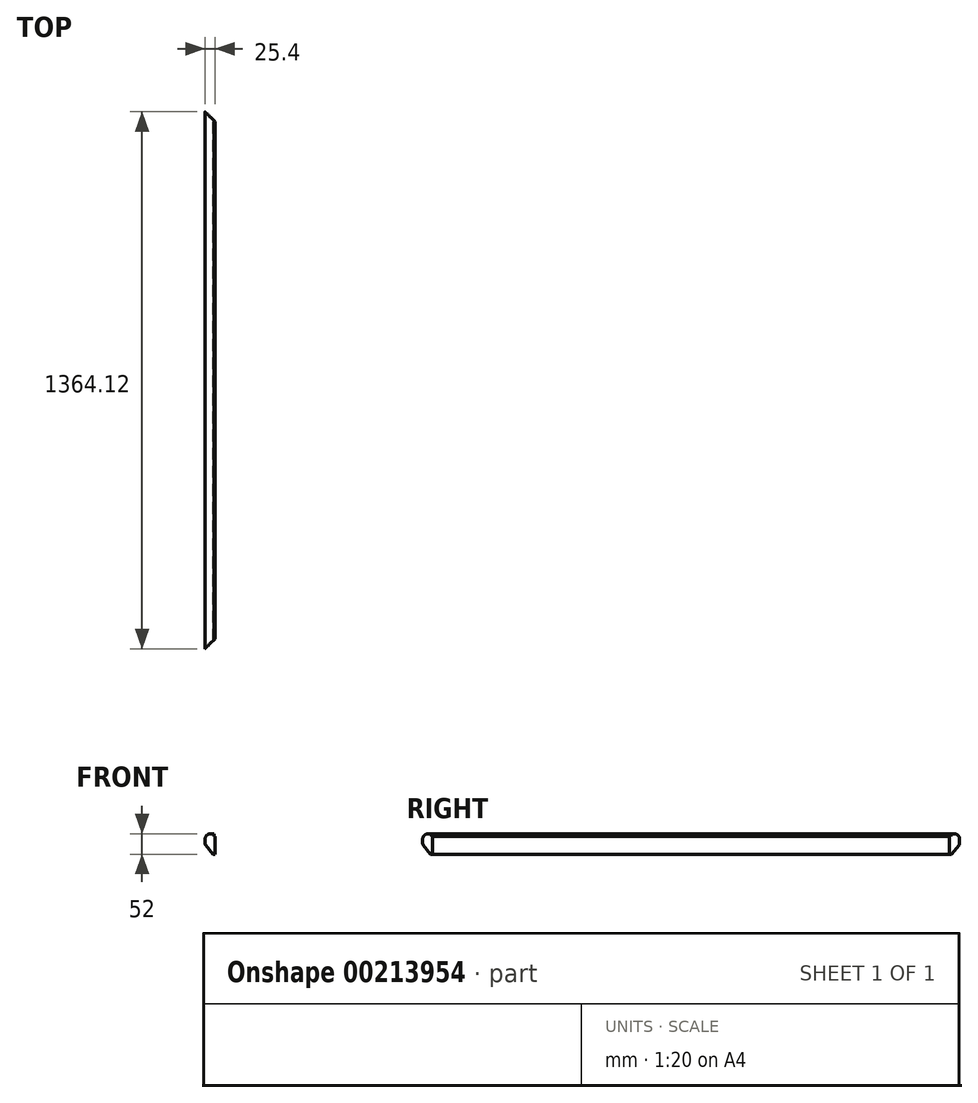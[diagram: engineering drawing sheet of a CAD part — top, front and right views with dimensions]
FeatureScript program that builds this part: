
annotation { "Feature Type Name" : "Feature", "Feature Type Description" : "" }
export const myFeature = defineFeature(function(context is Context, id is Id, definition is map)
    precondition{}
    {
        {
            var Q0;
            Q0=qCreatedBy(makeId("Front.planeOp"),FACE);
            var sketch = newSketch(context, id + "F0", { "sketchPlane" : qUnion([Q0])});
            skLineSegment(sketch, "E0.bottom", {"start": v(-11.4, 0) * mm, "end": v(-3, 0) * mm});
            skLineSegment(sketch, "E0.top", {"start": v(-5, -52) * mm, "end": v(0, -52) * mm});
            skLineSegment(sketch, "E0.left", {"start": v(-25.4, -14) * mm, "end": v(-25.4, -25.22) * mm});
            skLineSegment(sketch, "E0.right", {"start": v(0, -7) * mm, "end": v(0, -52) * mm});
            skLineSegment(sketch, "E1", {"start": v(-24.27, -28.38) * mm, "end": v(-5, -52) * mm});
            skPoint(sketch, "E2.visualSharp", {"position": v(-25.4, 0) * mm});
            skArc(sketch, "E2.filletArc", {"start": v(-11.4, 0) * mm, "mid": v(-21.3, -4.1) * mm, "end": v(-25.4, -14) * mm});
            skPoint(sketch, "E3.visualSharp", {"position": v(-25.4, -27) * mm});
            skArc(sketch, "E3.filletArc", {"start": v(-25.4, -25.22) * mm, "mid": v(-25.11, -26.9) * mm, "end": v(-24.27, -28.38) * mm});
            skLineSegment(sketch, "E4.top", {"start": v(-3, -7) * mm, "end": v(0, -7) * mm});
            skLineSegment(sketch, "E4.left", {"start": v(-3, 0) * mm, "end": v(-3, -7) * mm});
            skPoint(sketch, "E5.orphan", {"position": v(0, 0) * mm});
            skSolve(sketch);
        }
        {
            var Q0;
            Q0 = qSketchRegion(id + "F0", true);
            extrude(context, id + "F1", {"entities" : qUnion([Q0]), "depth" : 1400 * mm});
        }
        {
            var Q0;
            Q0=makeQuery(id+"F1.opExtrude","SWEPT_FACE",FACE,{"disambiguationData":[OSD([sQuery(id+"F0.wireOp",EDGE,"E0.bottom")])]});
            var sketch = newSketch(context, id + "F2", { "sketchPlane" : qUnion([Q0])});
            skLineSegment(sketch, "E6", {"start": v(-25.4, 0) * mm, "end": v(0, -25.4) * mm});
            skLineSegment(sketch, "E7", {"start": v(-25.4, 0) * mm, "end": v(-25.4, 2.43) * mm});
            skLineSegment(sketch, "E8", {"start": v(-25.4, 2.43) * mm, "end": v(2.47, 2.43) * mm});
            skPoint(sketch, "E9.orphan", {"position": v(0, 0) * mm});
            skPoint(sketch, "E10.0.start.orphan", {"position": v(0, -1400) * mm});
            skLineSegment(sketch, "E11", {"start": v(0, -25.4) * mm, "end": v(0, 0) * mm});
            skLineSegment(sketch, "E12", {"start": v(0, 0) * mm, "end": v(2.47, 2.43) * mm});
            skLineSegment(sketch, "E13", {"start": v(0, -1338.72) * mm, "end": v(-53.2, -1391.92) * mm});
            skLineSegment(sketch, "E14", {"start": v(0, -1338.72) * mm, "end": v(12, -1377.65) * mm});
            skLineSegment(sketch, "E15", {"start": v(12, -1377.65) * mm, "end": v(5.71, -1417.38) * mm});
            skLineSegment(sketch, "E16", {"start": v(5.71, -1417.38) * mm, "end": v(-53.2, -1391.92) * mm});
            skSolve(sketch);
        }
        {
            var Q0;
            Q0 = qSketchRegion(id + "F2", true);
            extrude(context, id + "F3", {"entities" : qUnion([Q0]), "operationType" : NewBodyOperationType.REMOVE, "endBound" : BoundingType.THROUGH_ALL, "oppositeDirection" : true, "depth" : 25 * mm});
        }
    });
